# Revit family: SOLD
name_source: partatom
category: Lighting Fixtures
revit_build: Autodesk Revit 2014 (Build: 20130308_1515(x64)
units: mm (PartAtom-declared; Revit-internal decimal feet)

## types (1)
- SOLD
    Apparent Load = 75 VA
    Assembly Code = D5020200
    Color Filter = 16777215
    Connector Description = Lighting Connector
    Default Elevation = 1219.2 mm  [stored 4 ft]
    Description = The unique characteristics of the Solas offers a versatile luminaire
with 100% output in emergency mode. Built in marine grade
aluminium this robust luminaire is suitable for the harshest of
global environments.
Utilising ultra bright LED’s the Solas produces a more focused light
well suited to illuminating safety critical areas in an emergency
situation. A manually operated remote inhibition facility is available
on all emergency versions. With a self contained battery, it can
be used for backup emergency lighting in maintained or nonmaintained modes.
    Dimming Lamp Color Temperature Shift = <None>
    Emit Shape Visible in Rendering = No
    Emit from Circle Diameter = 250 mm  [stored 0.82021 ft]
    Features = Highly Energy Efficient Comparable with 100W HPS floodlight
Emergency inhibition Non-Maintained or Maintained modes
Ex e terminal chamber No re-lamping required - over 80,000 hours continuous operation
Low ambient temperatures
    Fixture distribution = Direct
    Glass = Hubbell - Glass
    Height = 535 mm
    Housing Material = Paint - Hubbell - White Texture
    IP Rating = IP66/67
    Inner Length = 420 mm  [stored 1.37795 ft]
    Lamp = LED
    Length = 445 mm  [stored 1.45997 ft]
    Load Classification = Lighting
    Manufacturer = Chalmit
    Model = SOLD
    Mounting = Paint - Hubbell - Light Silver
    Photometric Web File = CHL_SOLD_034_LE_EM.ies
    Power Factor = 1
    Product Documentation Link = https://hubbellcdn.com
    Product Link = https://www.hubbell.com
    Reflector Finish = Hubbell - White Glass
    Tilt Angle = 90.00°
    URL = https://www.hubbell.com
    Voltage = 120 V
    Warranty = 5 years Warranty
    Wattage Comments = 75W
    Watts = 75 W
    Width = 280 mm  [stored 0.918635 ft]
    Wings = Paint - Hubbell - Light Silver

note: [stored X ft] marks values corroborated as IEEE doubles in the binary element streams (Revit-internal decimal feet)

## geometry (parser evidence)
native form markers: Sweep x2
no freeform markers — native parametric forms only
